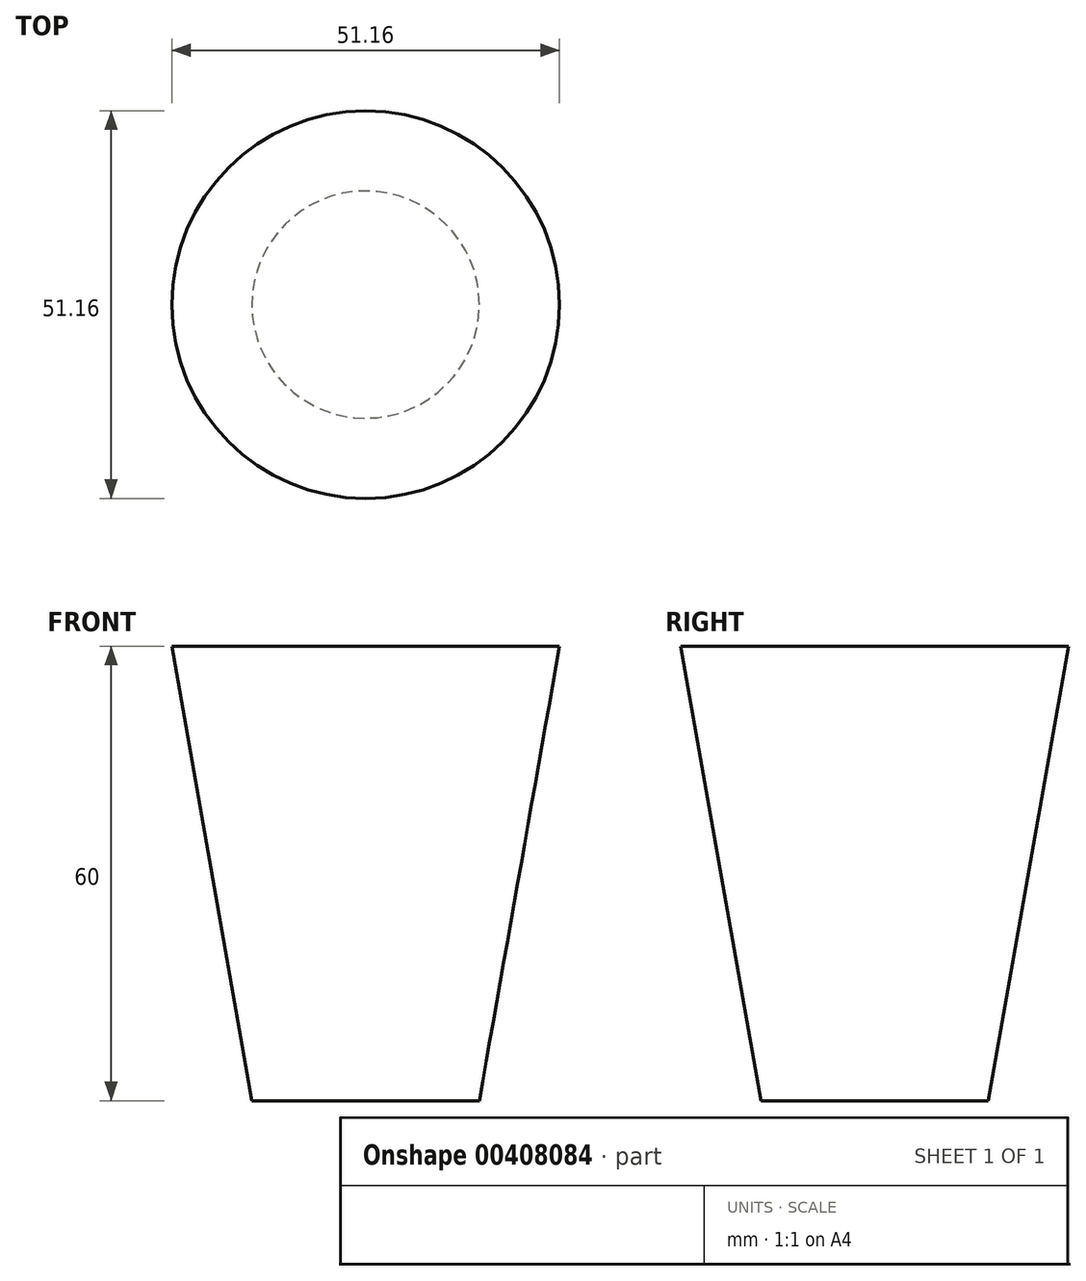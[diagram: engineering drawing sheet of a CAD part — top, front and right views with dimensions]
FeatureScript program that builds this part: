
annotation { "Feature Type Name" : "Feature", "Feature Type Description" : "" }
export const myFeature = defineFeature(function(context is Context, id is Id, definition is map)
    precondition{}
    {
        {
            var Q0;
            Q0=qCreatedBy(makeId("Top.planeOp"),FACE);
            var sketch = newSketch(context, id + "F0", { "sketchPlane" : qUnion([Q0])});
            skCircle(sketch, "E0", {"center": v(0, 0) * mm, "radius": 15 * mm});
            skSolve(sketch);
        }
        {
            var Q0;
            Q0=makeQuery(id+"F0.imprint","IMPRINT",FACE,{"disambiguationData":[TD([[makeQuery(id+"F0.imprint","IMPRINT",EDGE,{"derivedFrom":sQuery(id+"F0.wireOp",EDGE,"E0")}),1.0]])]});
            var Q1;
            Q1=sQuery(id+"F0.wireOp",EDGE,"E0");
            extrude(context, id + "F1", {"entities" : qUnion([Q0]), "surfaceEntities" : qUnion([Q1]), "depth" : 60 * mm, "hasDraft" : true, "draftAngle" : 10 * degree});
        }
    });
